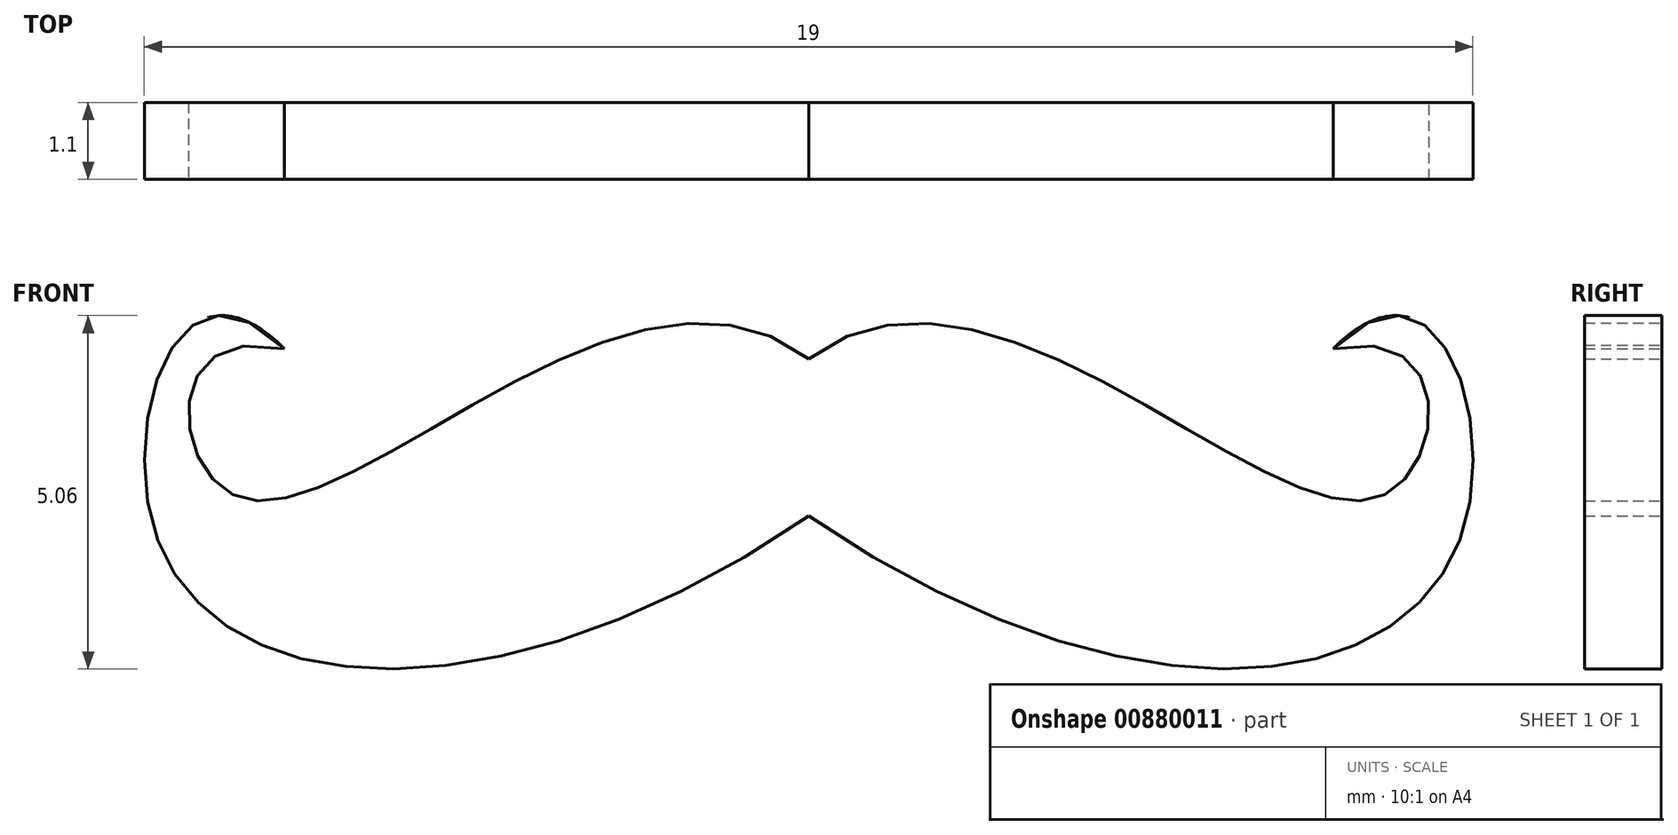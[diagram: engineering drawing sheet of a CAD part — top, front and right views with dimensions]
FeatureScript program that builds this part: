
annotation { "Feature Type Name" : "Feature", "Feature Type Description" : "" }
export const myFeature = defineFeature(function(context is Context, id is Id, definition is map)
    precondition{}
    {
        {
            var Q0;
            Q0=qCreatedBy(makeId("Front.planeOp"),FACE);
            var sketch = newSketch(context, id + "F0", { "sketchPlane" : qUnion([Q0])});
            skLineSegment(sketch, "E0.bottom", {"start": v(-67.3, -64.67) * mm, "end": v(67.3, -64.67) * mm});
            skLineSegment(sketch, "E0.top", {"start": v(-67.3, 64.67) * mm, "end": v(67.3, 64.67) * mm});
            skLineSegment(sketch, "E0.left", {"start": v(-67.3, -64.67) * mm, "end": v(-67.3, 64.67) * mm});
            skLineSegment(sketch, "E0.right", {"start": v(67.3, -64.67) * mm, "end": v(67.3, 64.67) * mm});
            skPoint(sketch, "E0.middle", {"position": v(0, 0) * mm});
            skFitSpline(sketch, "E1", {"points": [v(-1.95, -1.08) * mm, v(7.47, -1.08) * mm, v(5.55, 1.32) * mm], "startDerivative": vector(21.32, -14.61) * mm, "endDerivative": vector(-12.19, -12.19) * mm});
            skFitSpline(sketch, "E2", {"points": [v(5.55, 1.32) * mm, v(6.33, -0.76) * mm, v(-2.21, 0.94) * mm], "startDerivative": vector(15.78, 3.36) * mm, "endDerivative": vector(-12.03, -11.88) * mm});
            skLineSegment(sketch, "E3", {"start": v(-1.95, 1.17) * mm, "end": v(-1.95, -1.08) * mm, "construction": true});
            skLineSegment(sketch, "E4", {"start": v(-1.95, 11.4) * mm, "end": v(-1.95, -13.57) * mm, "construction": true});
            skFitSpline(sketch, "E5.MirrorCS", {"points": [v(-1.95, -1.08) * mm, v(-11.36, -1.08) * mm, v(-9.45, 1.32) * mm], "startDerivative": vector(-21.32, -14.61) * mm, "endDerivative": vector(12.19, -12.19) * mm});
            skFitSpline(sketch, "E6.MirrorCS", {"points": [v(-9.45, 1.32) * mm, v(-10.22, -0.76) * mm, v(-1.68, 0.94) * mm], "startDerivative": vector(-15.78, 3.36) * mm, "endDerivative": vector(12.03, -11.88) * mm});
            skSolve(sketch);
        }
        {
            var Q0;
            Q0=makeQuery(id+"F0.imprint","IMPRINT",FACE,{"disambiguationData":[TD([[makeQuery(id+"F0.imprint","IMPRINT",EDGE,{"derivedFrom":sQuery(id+"F0.wireOp",EDGE,"E1")}),1.0]])]});
            extrude(context, id + "F1", {"entities" : qUnion([Q0]), "depth" : 1.1 * mm, "offsetDistance" : 25 * mm});
        }
    });
